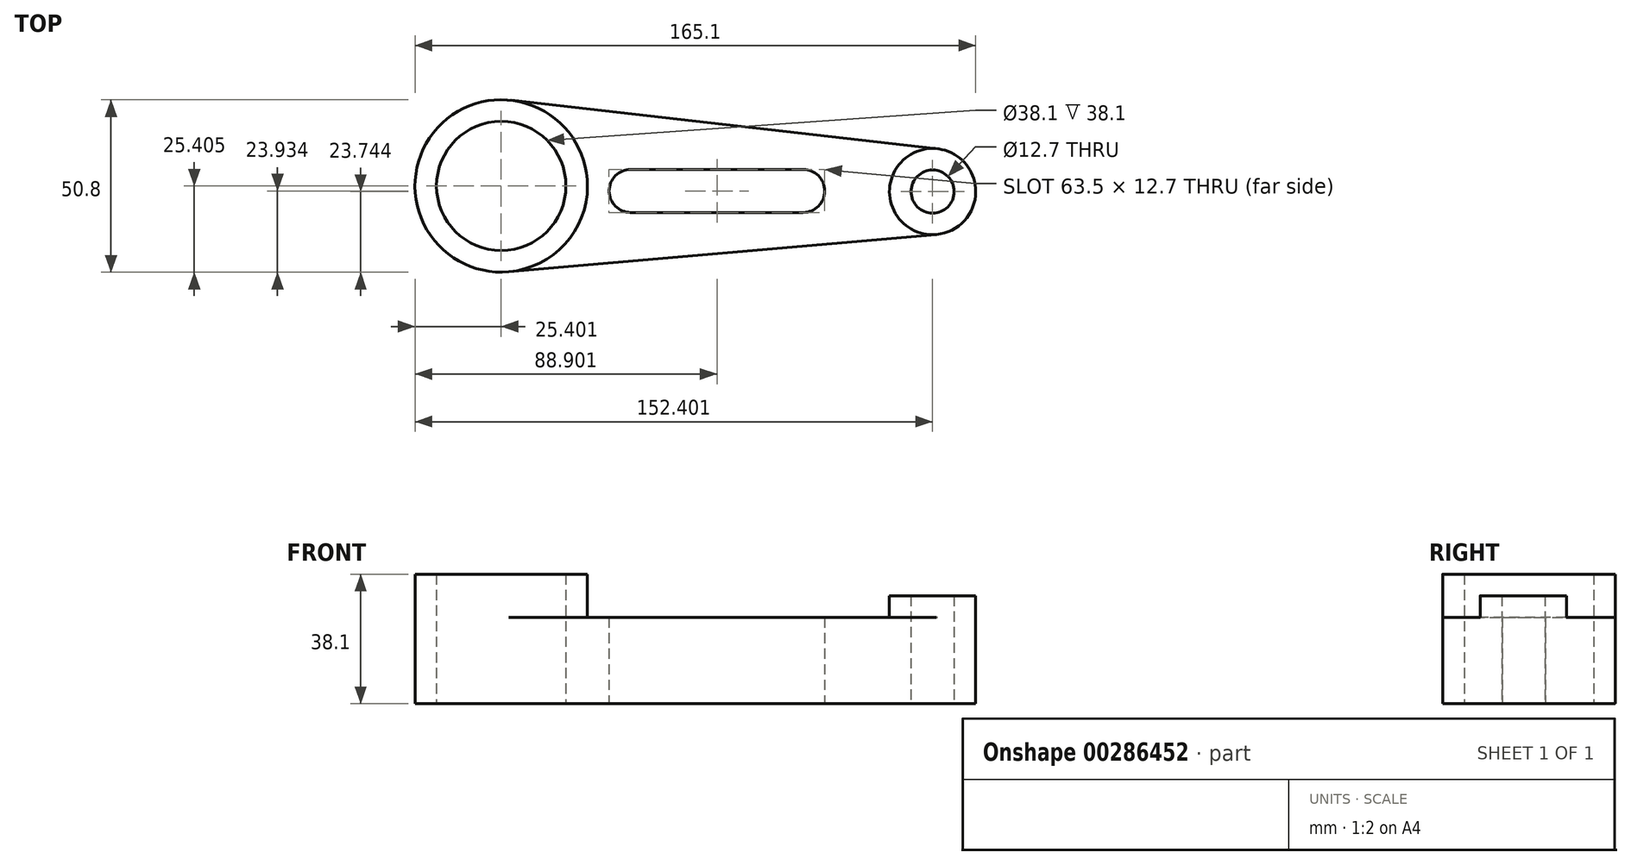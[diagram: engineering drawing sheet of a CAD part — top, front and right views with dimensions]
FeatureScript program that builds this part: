
annotation { "Feature Type Name" : "Feature", "Feature Type Description" : "" }
export const myFeature = defineFeature(function(context is Context, id is Id, definition is map)
    precondition{}
    {
        {
            var Q0;
            Q0=qCreatedBy(makeId("Top.planeOp"),FACE);
            var sketch = newSketch(context, id + "F0", { "sketchPlane" : qUnion([Q0])});
            skCircle(sketch, "E0", {"center": v(-95.9, 13.23) * mm, "radius": 19.05 * mm});
            skCircle(sketch, "E1", {"center": v(-95.9, 13.23) * mm, "radius": 25.4 * mm});
            skCircle(sketch, "E2", {"center": v(31.1, 11.57) * mm, "radius": 6.35 * mm});
            skCircle(sketch, "E3", {"center": v(31.1, 11.57) * mm, "radius": 12.7 * mm});
            skLineSegment(sketch, "E4", {"start": v(-93.03, 38.47) * mm, "end": v(32.54, 24.2) * mm});
            skLineSegment(sketch, "E5", {"start": v(-93.69, -12.07) * mm, "end": v(32.2, -1.08) * mm});
            skLineSegment(sketch, "E6.bottom", {"start": v(-57.8, 18.11) * mm, "end": v(-7, 18.11) * mm});
            skLineSegment(sketch, "E6.top", {"start": v(-57.8, 5.41) * mm, "end": v(-7, 5.41) * mm});
            skArc(sketch, "E7", {"start": v(-7, 5.41) * mm, "mid": v(-0.65, 11.76) * mm, "end": v(-7, 18.11) * mm});
            skArc(sketch, "E8", {"start": v(-57.8, 18.11) * mm, "mid": v(-64.15, 11.76) * mm, "end": v(-57.8, 5.41) * mm});
            skSolve(sketch);
        }
        {
            var Q0;
            Q0=makeQuery(id+"F0.imprint","IMPRINT",FACE,{"disambiguationData":[TD([[makeQuery(id+"F0.imprint","IMPRINT",EDGE,{"derivedFrom":sQuery(id+"F0.wireOp",EDGE,"E0")}),-1.0]])]});
            extrude(context, id + "F1", {"entities" : qUnion([Q0]), "depth" : 38.1 * mm});
        }
        {
            var Q0;
            Q0=makeQuery(id+"F0.imprint","IMPRINT",FACE,{"disambiguationData":[TD([[makeQuery(id+"F0.imprint","IMPRINT",EDGE,{"derivedFrom":sQuery(id+"F0.wireOp",EDGE,"E2")}),-1.0]])]});
            extrude(context, id + "F2", {"entities" : qUnion([Q0]), "operationType" : NewBodyOperationType.ADD, "depth" : 31.75 * mm});
        }
        {
            var Q0;
            {var subQ0=sQuery(id+"F0.wireOp",EDGE,"E4");Q0=makeQuery(id+"F0.imprint","IMPRINT",FACE,{"disambiguationData":[TD([[makeQuery(id+"F0.imprint","IMPRINT",EDGE,{"derivedFrom":subQ0}),-1.0]])]});}
            extrude(context, id + "F3", {"entities" : qUnion([Q0]), "operationType" : NewBodyOperationType.ADD, "depth" : 25.4 * mm});
        }
    });
